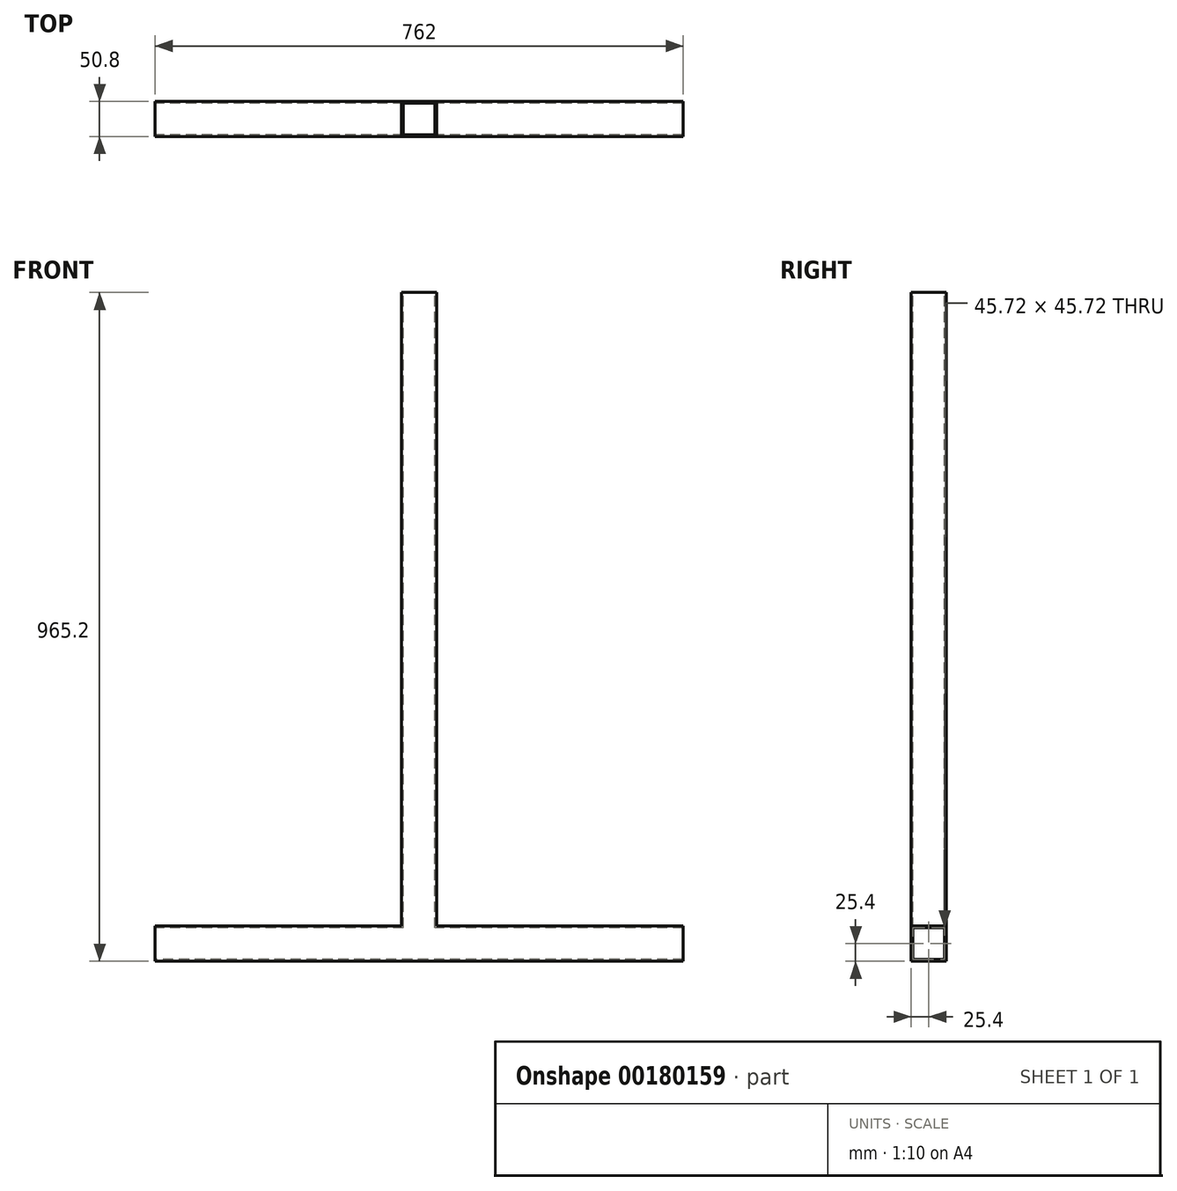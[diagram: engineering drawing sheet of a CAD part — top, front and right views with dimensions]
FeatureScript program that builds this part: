
annotation { "Feature Type Name" : "Feature", "Feature Type Description" : "" }
export const myFeature = defineFeature(function(context is Context, id is Id, definition is map)
    precondition{}
    {
        {
            var Q0;
            Q0=qCreatedBy(makeId("Front.planeOp"),FACE);
            var sketch = newSketch(context, id + "F0", { "sketchPlane" : qUnion([Q0])});
            skLineSegment(sketch, "E0.bottom", {"start": v(0, 0) * mm, "end": v(50.8, 0) * mm});
            skLineSegment(sketch, "E0.top", {"start": v(0, 914.4) * mm, "end": v(50.8, 914.4) * mm});
            skLineSegment(sketch, "E0.left", {"start": v(0, 0) * mm, "end": v(0, 914.4) * mm});
            skLineSegment(sketch, "E0.right", {"start": v(50.8, 0) * mm, "end": v(50.8, 914.4) * mm});
            skLineSegment(sketch, "E1.bottom", {"start": v(406.4, 0) * mm, "end": v(-355.6, 0) * mm});
            skLineSegment(sketch, "E1.top", {"start": v(406.4, -50.8) * mm, "end": v(-355.6, -50.8) * mm});
            skLineSegment(sketch, "E1.left", {"start": v(406.4, 0) * mm, "end": v(406.4, -50.8) * mm});
            skLineSegment(sketch, "E1.right", {"start": v(-355.6, 0) * mm, "end": v(-355.6, -50.8) * mm});
            skSolve(sketch);
        }
        {
            var Q0;
            Q0=makeQuery(id+"F0.imprint","IMPRINT",FACE,{"disambiguationData":[TD([[makeQuery(id+"F0.imprint","IMPRINT",EDGE,{"derivedFrom":sQuery(id+"F0.wireOp",EDGE,"E0.top")}),-1.0]])]});
            var Q1;
            Q1=makeQuery(id+"F0.imprint","IMPRINT",FACE,{"disambiguationData":[TD([[makeQuery(id+"F0.imprint","IMPRINT",EDGE,{"derivedFrom":sQuery(id+"F0.wireOp",EDGE,"E1.top")}),-1.0]])]});
            extrude(context, id + "F1", {"entities" : qUnion([Q0, Q1]), "depth" : 50.8 * mm});
        }
        {
            var Q0;
            Q0=makeQuery(id+"F1.opExtrude","SWEPT_FACE",FACE,{"disambiguationData":[OSD([sQuery(id+"F0.wireOp",EDGE,"E0.top")])]});
            var Q1;
            Q1=makeQuery(id+"F1.opExtrude","SWEPT_FACE",FACE,{"disambiguationData":[OSD([sQuery(id+"F0.wireOp",EDGE,"E1.left")])]});
            var Q2;
            Q2=makeQuery(id+"F1.opExtrude","SWEPT_FACE",FACE,{"disambiguationData":[OSD([sQuery(id+"F0.wireOp",EDGE,"E1.right")])]});
            shell(context, id + "F2", {"entities" : qUnion([Q0, Q1, Q2]), "thickness" : 2.54 * mm});
        }
    });
